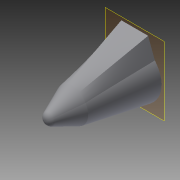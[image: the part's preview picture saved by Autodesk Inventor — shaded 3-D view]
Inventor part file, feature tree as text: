
AUTODESK INVENTOR PART (.ipt)
format: ipt  version: 2015 (Build 190159000, 159)  size: 215,552 bytes
history: native  units: in
note: dims shown in document units (in); Inventor stores cm internally (conversion verified against a paired STEP export)
features: sketch x6, loft x3, plane x2, fillet x1, projected_geometry x1, other x1
ambient origin geometry x8: Origin, YZ Plane, XZ Plane, XY Plane, X Axis, Y Axis, Z Axis, Center Point
bodies: Solid1 (feature_tree)
feature tree (14):
  sketch  "Sketch1"  dims[d0=1.75in d1=0.9in]
  plane  "Work Plane1"
  sketch  "Sketch2"  dims[d4=0.42in d5=0.0in d6=90.0deg]
  sketch  "Sketch3"  dims[d7=0.0in d8=90.0deg d9=0.45in d10=0.0in d11=90.0deg]
  sketch  "Sketch4"  dims[d12=0.0in d13=90.0deg]
  loft  "Loft1"
  loft  "Loft2"
  sketch  "Sketch5"  dims[d14=0.0in]
  plane  "Work Plane2"
  loft  "Loft3"
  fillet  "Fillet1"  [1 undecoded]
  projected_geometry  "Projected Loop1"
  sketch  "Sketch6"  dims[d15=0.75in d16=0.0in d17=90.0deg d18=0.0in d19=90.0deg d20=0.1731in]
  other  "Edges1"
note: 1 required parameter value undecoded (feature->parameter linkage not recoverable at this tier; creation-order binding heuristic only, values carry confidence <= 0.55)
